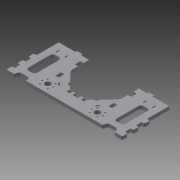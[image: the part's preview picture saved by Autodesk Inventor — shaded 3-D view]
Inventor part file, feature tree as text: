
AUTODESK INVENTOR PART (.ipt)
format: ipt  version: 2015 (Build 190159000, 159)  size: 382,976 bytes
history: native  units: mm
features: extrude x6, sketch x5, fillet x3
ambient origin geometry x8: Origin, YZ Plane, XZ Plane, XY Plane, X Axis, Y Axis, Z Axis, Center Point
bodies: Solid1 (feature_tree)
feature tree (14):
  extrude  "Extrusion1"  Depth=10.0mm
  extrude  "Extrusion2"  Depth=90.0mm
  extrude  "Extrusion5"  Depth=10.0mm
  sketch  "Sketch3"  dims[d6=5.0mm d7=90.0mm]
  extrude  "Extrusion13"  Depth=10.0mm
  fillet  "Fillet4"  Radius=30.0mm
  fillet  "Fillet5"  Radius=10.0mm
  extrude  "Extrusion15"  Depth=90.0mm
  fillet  "Fillet7"  Radius=15.0mm
  extrude  "Extrusion16"  Depth=18.0mm
  sketch  "Sketch2"  dims[d4=105.0mm d5=10.0mm]
  sketch  "Sketch5"  dims[d8=10.0mm d9=10.0mm]
  sketch  "Sketch7"  dims[d10=10.0mm d11=10.0mm d12=30.0mm d13=10.0mm]
  sketch  "Sketch8"  dims[d14=3.0mm d15=90.0mm d18=15.0mm d19=34.0mm d20=2.0mm d21=6.0mm d22=0.0mm d23=10.0mm d25=75.0mm d26=45.0mm d27=20.0mm d28=45.0deg d29=2.5mm d30=2.5mm d31=6.0mm d32=0.0mm d41=6.0mm d43=12.0mm d65=5.0mm d66=6.0mm d67=0.0mm d77=68.0mm d102=5.0mm d104=5.0mm d105=10.0mm d129=12.0mm d130=14.0mm d131=2.0mm d132=2.0mm d135=10.0mm d136=8.0mm d137=20.0mm d138=10.0mm d139=20.0mm d140=8.0mm d141=10.0mm d142=0.0mm d143=5.0mm d144=2.0mm d160=6.0mm d161=6.0mm d162=6.0mm d163=70.0mm d165=3.0mm d166=3.0mm d167=2.0mm d168=11.0mm d170=2.0mm d171=3.0mm d172=3.0mm d173=10.0mm d174=0.0mm d175=10.0mm d176=0.5mm d177=6.0mm d178=10.0mm d179=10.0mm d180=10.0mm d181=6.0mm d182=55.0mm d183=6.0mm d184=10.0mm d185=10.0mm d186=0.0mm d187=23.0mm d188=12.0mm d189=16.0mm d190=18.0mm]
